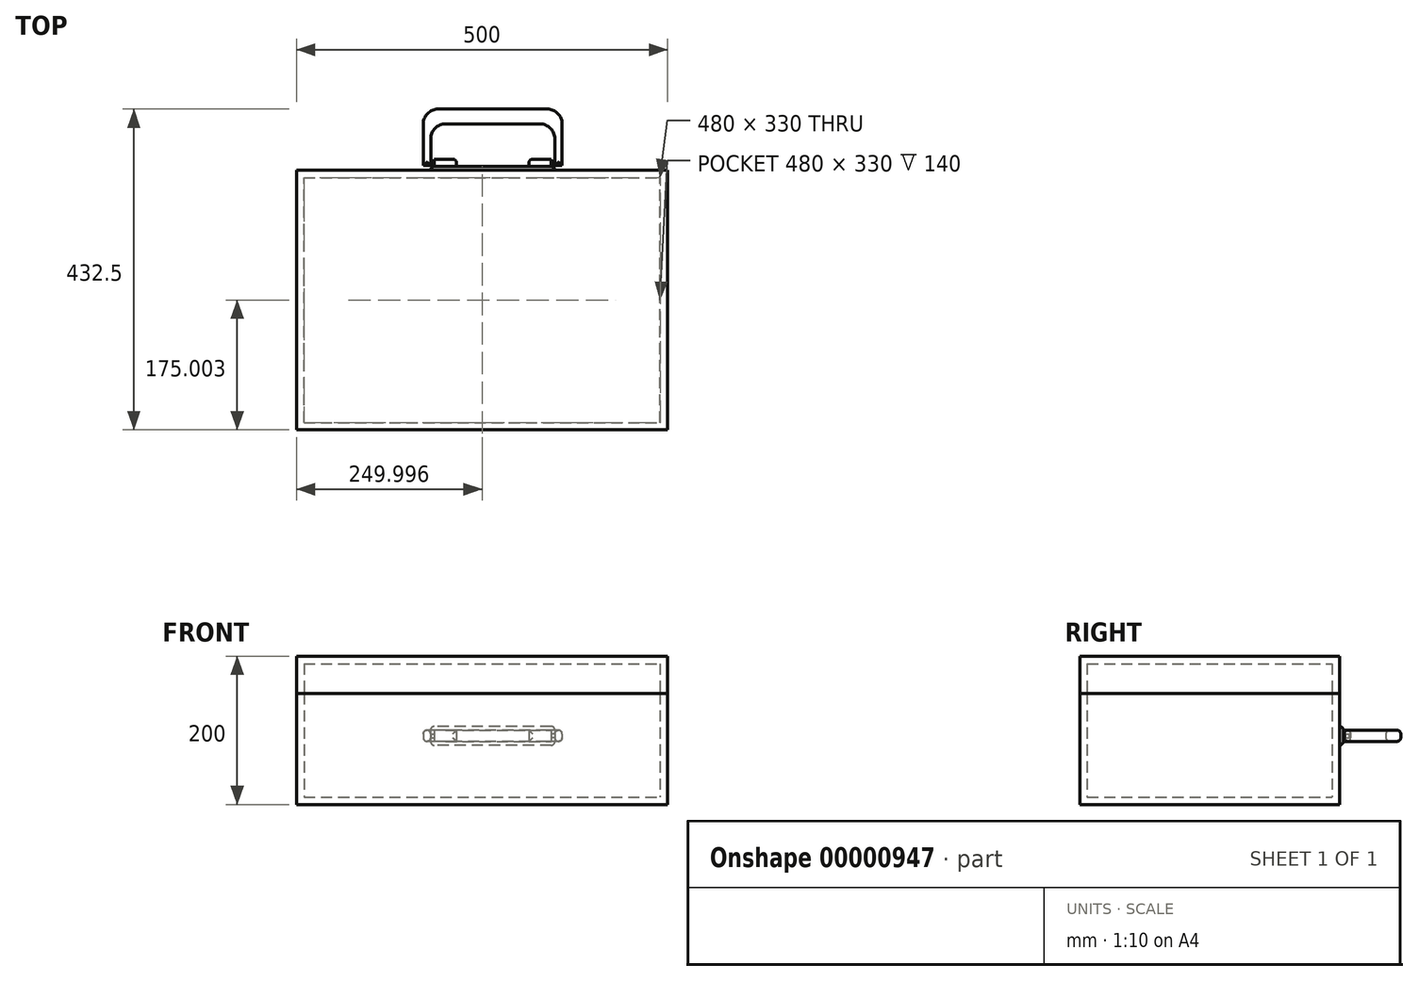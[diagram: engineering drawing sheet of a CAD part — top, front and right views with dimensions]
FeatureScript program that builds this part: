
annotation { "Feature Type Name" : "Feature", "Feature Type Description" : "" }
export const myFeature = defineFeature(function(context is Context, id is Id, definition is map)
    precondition{}
    {
        {
            var Q0;
            Q0=qCreatedBy(makeId("Top.planeOp"),FACE);
            var sketch = newSketch(context, id + "F0", { "sketchPlane" : qUnion([Q0])});
            skLineSegment(sketch, "E0.bottom", {"start": v(-264.32, -184.4) * mm, "end": v(235.68, -184.4) * mm});
            skLineSegment(sketch, "E0.top", {"start": v(-264.32, 165.6) * mm, "end": v(235.68, 165.6) * mm});
            skLineSegment(sketch, "E0.left", {"start": v(-264.32, -184.4) * mm, "end": v(-264.32, 165.6) * mm});
            skLineSegment(sketch, "E0.right", {"start": v(235.68, -184.4) * mm, "end": v(235.68, 165.6) * mm});
            skSolve(sketch);
        }
        {
            var Q0;
            Q0=makeQuery(id+"F0.imprint","IMPRINT",FACE,{"disambiguationData":[TD([[makeQuery(id+"F0.imprint","IMPRINT",EDGE,{"derivedFrom":sQuery(id+"F0.wireOp",EDGE,"E0.bottom")}),1.0]])]});
            extrude(context, id + "F1", {"entities" : qUnion([Q0]), "depth" : 150 * mm});
        }
        {
            var Q0;
            Q0=makeQuery(id+"F1.opExtrude","CAP_FACE",FACE,{"disambiguationData":[OSD([sQuery(id+"F0.wireOp",EDGE,"E0.bottom"),sQuery(id+"F0.wireOp",EDGE,"E0.top"),sQuery(id+"F0.wireOp",EDGE,"E0.left"),sQuery(id+"F0.wireOp",EDGE,"E0.right")])],"isStart":false});
            shell(context, id + "F2", {"entities" : qUnion([Q0]), "thickness" : 10 * mm});
        }
        {
            var Q0;
            Q0=makeQuery(id+"F1.opExtrude","CAP_FACE",FACE,{"disambiguationData":[OSD([sQuery(id+"F0.wireOp",EDGE,"E0.bottom"),sQuery(id+"F0.wireOp",EDGE,"E0.top"),sQuery(id+"F0.wireOp",EDGE,"E0.left"),sQuery(id+"F0.wireOp",EDGE,"E0.right")])],"isStart":false});
            var sketch = newSketch(context, id + "F3", { "sketchPlane" : qUnion([Q0])});
            skLineSegment(sketch, "E1.0", {"start": v(-264.32, 165.6) * mm, "end": v(235.68, 165.6) * mm});
            skLineSegment(sketch, "E2.0", {"start": v(-264.32, -184.4) * mm, "end": v(-264.32, 165.6) * mm});
            skLineSegment(sketch, "E3.0", {"start": v(235.68, -184.4) * mm, "end": v(235.68, 165.6) * mm});
            skLineSegment(sketch, "E4.0", {"start": v(-264.32, -184.4) * mm, "end": v(235.68, -184.4) * mm});
            skSolve(sketch);
        }
        {
            var Q0;
            {var subQ6=sQuery(id+"F0.wireOp",EDGE,"E0.bottom");var subQ7=makeQuery(id+"F3.imprint","IMPRINT",EDGE,{"derivedFrom":makeQuery(id+"F2.opShell","OFFSET_EDGE",EDGE,{"disambiguationData":[OSD([subQ6]),TDD([makeQuery(id+"F1.opExtrude","CAP_EDGE",EDGE,{"disambiguationData":[OSD([subQ6])],"isStart":false})])]})});Q0=qUnion([makeQuery(id+"F3.imprint","IMPRINT",FACE,{"disambiguationData":[TD([[makeQuery(id+"F3.imprint","IMPRINT",EDGE,{"derivedFrom":sQuery(id+"F3.wireOp",EDGE,"E1.0")}),-1.0]])]}),makeQuery(id+"F3.imprint","IMPRINT",FACE,{"disambiguationData":[TD([[subQ7,1.0]])]})]);}
            extrude(context, id + "F4", {"entities" : qUnion([Q0]), "depth" : 50 * mm});
        }
        {
            var Q0;
            Q0=makeQuery(id+"F4.opExtrude","CAP_FACE",FACE,{"disambiguationData":[OSD([sQuery(id+"F3.wireOp",EDGE,"E1.0"),sQuery(id+"F3.wireOp",EDGE,"E2.0"),sQuery(id+"F3.wireOp",EDGE,"E3.0"),sQuery(id+"F3.wireOp",EDGE,"E4.0")])],"isStart":true});
            shell(context, id + "F5", {"entities" : qUnion([Q0]), "thickness" : 10 * mm});
        }
        {
            var Q0;
            Q0=makeQuery(id+"F1.opExtrude","SWEPT_FACE",FACE,{"disambiguationData":[OSD([sQuery(id+"F0.wireOp",EDGE,"E0.top")])]});
            var sketch = newSketch(context, id + "F6", { "sketchPlane" : qUnion([Q0])});
            skLineSegment(sketch, "E5.rect.bottom", {"start": v(-78.8, 105.28) * mm, "end": v(78.8, 105.28) * mm});
            skLineSegment(sketch, "E5.rect.top", {"start": v(-78.8, 79.98) * mm, "end": v(78.8, 79.98) * mm});
            skLineSegment(sketch, "E5.rect.left", {"start": v(-83.8, 100.28) * mm, "end": v(-83.8, 84.98) * mm});
            skLineSegment(sketch, "E5.rect.right", {"start": v(83.8, 100.28) * mm, "end": v(83.8, 84.98) * mm});
            skPoint(sketch, "E5.rect.middle", {"position": v(0, 92.63) * mm});
            skPoint(sketch, "E6.visualSharp", {"position": v(-83.8, 105.28) * mm});
            skArc(sketch, "E6.filletArc", {"start": v(-78.8, 105.28) * mm, "mid": v(-82.33, 103.81) * mm, "end": v(-83.8, 100.28) * mm});
            skPoint(sketch, "E7.visualSharp", {"position": v(-83.8, 79.98) * mm});
            skArc(sketch, "E7.filletArc", {"start": v(-83.8, 84.98) * mm, "mid": v(-82.33, 81.45) * mm, "end": v(-78.8, 79.98) * mm});
            skPoint(sketch, "E8.visualSharp", {"position": v(83.8, 79.98) * mm});
            skArc(sketch, "E8.filletArc", {"start": v(78.8, 79.98) * mm, "mid": v(82.33, 81.45) * mm, "end": v(83.8, 84.98) * mm});
            skPoint(sketch, "E9.visualSharp", {"position": v(83.8, 105.28) * mm});
            skArc(sketch, "E9.filletArc", {"start": v(83.8, 100.28) * mm, "mid": v(82.33, 103.81) * mm, "end": v(78.8, 105.28) * mm});
            skLineSegment(sketch, "E10.bottom", {"start": v(-48.8, 100.28) * mm, "end": v(-78.8, 100.28) * mm});
            skLineSegment(sketch, "E10.top", {"start": v(-48.8, 84.98) * mm, "end": v(-78.8, 84.98) * mm});
            skLineSegment(sketch, "E10.left", {"start": v(-48.8, 100.28) * mm, "end": v(-48.8, 84.98) * mm});
            skLineSegment(sketch, "E10.right", {"start": v(-78.8, 100.28) * mm, "end": v(-78.8, 84.98) * mm});
            skLineSegment(sketch, "E11", {"start": v(0, 79.98) * mm, "end": v(0, 105.28) * mm, "construction": true});
            skLineSegment(sketch, "E12.0.MirrorCS", {"start": v(48.8, 84.98) * mm, "end": v(78.8, 84.98) * mm});
            skLineSegment(sketch, "E13.0.MirrorCS", {"start": v(48.8, 100.28) * mm, "end": v(48.8, 84.98) * mm});
            skLineSegment(sketch, "E14.0.MirrorCS", {"start": v(48.8, 100.28) * mm, "end": v(78.8, 100.28) * mm});
            skLineSegment(sketch, "E15.0.MirrorCS", {"start": v(78.8, 100.28) * mm, "end": v(78.8, 84.98) * mm});
            skSolve(sketch);
        }
        {
            var Q0;
            Q0=makeQuery(id+"F6.imprint","IMPRINT",FACE,{"disambiguationData":[TD([[makeQuery(id+"F6.imprint","IMPRINT",EDGE,{"derivedFrom":sQuery(id+"F6.wireOp",EDGE,"E5.rect.bottom")}),-1.0]])]});
            extrude(context, id + "F7", {"entities" : qUnion([Q0]), "depth" : 5 * mm});
        }
        {
            var Q0;
            Q0=makeQuery(id+"F6.imprint","IMPRINT",FACE,{"disambiguationData":[TD([[makeQuery(id+"F6.imprint","IMPRINT",EDGE,{"derivedFrom":sQuery(id+"F6.wireOp",EDGE,"E10.bottom")}),1.0]])]});
            var Q1;
            Q1=makeQuery(id+"F6.imprint","IMPRINT",FACE,{"disambiguationData":[TD([[makeQuery(id+"F6.imprint","IMPRINT",EDGE,{"derivedFrom":sQuery(id+"F6.wireOp",EDGE,"E12.0.MirrorCS")}),1.0]])]});
            extrude(context, id + "F8", {"entities" : qUnion([Q0, Q1]), "operationType" : NewBodyOperationType.ADD, "depth" : 15 * mm});
        }
        {
            var Q0;
            Q0=makeQuery(id+"F8.opExtrude","CAP_EDGE",EDGE,{"disambiguationData":[OSD([sQuery(id+"F6.wireOp",EDGE,"E10.top")])],"isStart":false});
            var Q1;
            Q1=makeQuery(id+"F8.opExtrude","CAP_EDGE",EDGE,{"disambiguationData":[OSD([sQuery(id+"F6.wireOp",EDGE,"E10.left")])],"isStart":false});
            var Q2;
            Q2=makeQuery(id+"F8.opExtrude","CAP_EDGE",EDGE,{"disambiguationData":[OSD([sQuery(id+"F6.wireOp",EDGE,"E10.bottom")])],"isStart":false});
            var Q3;
            Q3=makeQuery(id+"F8.opExtrude","CAP_EDGE",EDGE,{"disambiguationData":[OSD([sQuery(id+"F6.wireOp",EDGE,"E13.0.MirrorCS")])],"isStart":false});
            var Q4;
            Q4=makeQuery(id+"F8.opExtrude","CAP_EDGE",EDGE,{"disambiguationData":[OSD([sQuery(id+"F6.wireOp",EDGE,"E14.0.MirrorCS")])],"isStart":false});
            var Q5;
            Q5=makeQuery(id+"F8.opExtrude","CAP_EDGE",EDGE,{"disambiguationData":[OSD([sQuery(id+"F6.wireOp",EDGE,"E12.0.MirrorCS")])],"isStart":false});
            fillet(context, id + "F9", {"entities" : qUnion([Q0, Q1, Q2, Q3, Q4, Q5]), "radius" : 5 * mm, "allowEdgeOverflow" : false});
        }
        {
            var Q0;
            Q0=makeQuery(id+"F7.opExtrude","CAP_EDGE",EDGE,{"disambiguationData":[OSD([sQuery(id+"F6.wireOp",EDGE,"E5.rect.bottom")])],"isStart":false});
            fillet(context, id + "F10", {"entities" : qUnion([Q0]), "radius" : 5 * mm, "tangentPropagation" : true, "allowEdgeOverflow" : false});
        }
        {
            var Q0;
            Q0=makeQuery(id+"F8.opExtrude","SWEPT_FACE",FACE,{"disambiguationData":[OSD([sQuery(id+"F6.wireOp",EDGE,"E10.bottom")])]});
            var Q1;
            Q1=makeQuery(id+"F8.opExtrude","SWEPT_FACE",FACE,{"disambiguationData":[OSD([sQuery(id+"F6.wireOp",EDGE,"E10.top")])]});
            cPlane(context, id + "F11", {"entities" : qUnion([Q0, Q1]), "cplaneType" : CPlaneType.MID_PLANE, "offset" : 150 * mm, "width" : 150 * mm, "height" : 150 * mm});
        }
        {
            var Q0;
            Q0=qCreatedBy(id+"F11.planeOp",FACE);
            var sketch = newSketch(context, id + "F12", { "sketchPlane" : qUnion([Q0])});
            skLineSegment(sketch, "E16.0", {"start": v(78.8, 175.6) * mm, "end": v(78.8, 173.1) * mm});
            skLineSegment(sketch, "E17.0", {"start": v(78.8, 175.6) * mm, "end": v(78.8, 180.6) * mm});
            skLineSegment(sketch, "E18", {"start": v(78.8, 173.1) * mm, "end": v(83.58, 173.1) * mm});
            skLineSegment(sketch, "E19", {"start": v(83.58, 173.1) * mm, "end": v(83.58, 171.8) * mm});
            skLineSegment(sketch, "E20", {"start": v(83.58, 171.8) * mm, "end": v(93.58, 171.8) * mm});
            skLineSegment(sketch, "E21", {"start": v(93.58, 171.8) * mm, "end": v(93.58, 228.1) * mm});
            skLineSegment(sketch, "E22", {"start": v(73.58, 248.1) * mm, "end": v(0, 248.1) * mm});
            skLineSegment(sketch, "E23", {"start": v(0, 248.1) * mm, "end": v(0, 228.1) * mm});
            skLineSegment(sketch, "E24", {"start": v(0, 228.1) * mm, "end": v(63.58, 228.1) * mm});
            skLineSegment(sketch, "E25", {"start": v(83.58, 208.1) * mm, "end": v(83.58, 178.62) * mm});
            skLineSegment(sketch, "E26", {"start": v(83.58, 178.62) * mm, "end": v(83.58, 178.1) * mm});
            skLineSegment(sketch, "E27", {"start": v(83.58, 178.1) * mm, "end": v(78.8, 178.1) * mm});
            skLineSegment(sketch, "E28", {"start": v(0, 257.2) * mm, "end": v(0, 154.47) * mm, "construction": true});
            skLineSegment(sketch, "E29.0.MirrorCS", {"start": v(-73.58, 248.1) * mm, "end": v(0, 248.1) * mm});
            skLineSegment(sketch, "E30.0.MirrorCS", {"start": v(-93.58, 171.8) * mm, "end": v(-93.58, 228.1) * mm});
            skLineSegment(sketch, "E31.0.MirrorCS", {"start": v(-83.58, 171.8) * mm, "end": v(-93.58, 171.8) * mm});
            skLineSegment(sketch, "E32.0.MirrorCS", {"start": v(-78.8, 173.1) * mm, "end": v(-83.58, 173.1) * mm});
            skLineSegment(sketch, "E33.0.MirrorCS", {"start": v(-83.58, 173.1) * mm, "end": v(-83.58, 171.8) * mm});
            skLineSegment(sketch, "E34.0.MirrorCS", {"start": v(-83.58, 178.1) * mm, "end": v(-78.8, 178.1) * mm});
            skLineSegment(sketch, "E35.0.MirrorCS", {"start": v(-83.58, 208.1) * mm, "end": v(-83.58, 178.62) * mm});
            skLineSegment(sketch, "E36.0.MirrorCS", {"start": v(-83.58, 178.62) * mm, "end": v(-83.58, 178.1) * mm});
            skLineSegment(sketch, "E37.0.MirrorCS", {"start": v(0, 228.1) * mm, "end": v(-63.58, 228.1) * mm});
            skLineSegment(sketch, "E38.0.MirrorCS", {"start": v(-78.8, 175.6) * mm, "end": v(-78.8, 178.1) * mm});
            skLineSegment(sketch, "E39.0.MirrorCS", {"start": v(-78.8, 175.6) * mm, "end": v(-78.8, 173.1) * mm});
            skPoint(sketch, "E40.orphan", {"position": v(-78.8, 180.6) * mm});
            skLineSegment(sketch, "E41", {"start": v(-83.58, 178.1) * mm, "end": v(-83.58, 173.1) * mm});
            skLineSegment(sketch, "E42", {"start": v(83.58, 178.1) * mm, "end": v(83.58, 173.1) * mm});
            skPoint(sketch, "E43.visualSharp", {"position": v(83.58, 228.1) * mm});
            skArc(sketch, "E43.filletArc", {"start": v(83.58, 208.1) * mm, "mid": v(77.72, 222.24) * mm, "end": v(63.58, 228.1) * mm});
            skPoint(sketch, "E44.visualSharp", {"position": v(93.58, 248.1) * mm});
            skArc(sketch, "E44.filletArc", {"start": v(93.58, 228.1) * mm, "mid": v(87.72, 242.24) * mm, "end": v(73.58, 248.1) * mm});
            skPoint(sketch, "E45.visualSharp", {"position": v(-83.58, 228.1) * mm});
            skArc(sketch, "E45.filletArc", {"start": v(-63.58, 228.1) * mm, "mid": v(-77.72, 222.24) * mm, "end": v(-83.58, 208.1) * mm});
            skPoint(sketch, "E46.visualSharp", {"position": v(-93.58, 248.1) * mm});
            skArc(sketch, "E46.filletArc", {"start": v(-73.58, 248.1) * mm, "mid": v(-87.72, 242.24) * mm, "end": v(-93.58, 228.1) * mm});
            skSolve(sketch);
        }
        {
            var Q0;
            {var subQ1=sQuery(id+"F12.wireOp",EDGE,"E18");Q0=makeQuery(id+"F12.imprint","IMPRINT",FACE,{"disambiguationData":[TD([[makeQuery(id+"F12.imprint","IMPRINT",EDGE,{"derivedFrom":subQ1}),1.0]])]});}
            var Q1;
            Q1=makeQuery(id+"F12.imprint","IMPRINT",FACE,{"disambiguationData":[TD([[makeQuery(id+"F12.imprint","IMPRINT",EDGE,{"derivedFrom":sQuery(id+"F12.wireOp",EDGE,"E32.0.MirrorCS")}),-1.0]])]});
            extrude(context, id + "F13", {"entities" : qUnion([Q0, Q1]), "endBound" : BoundingType.SYMMETRIC, "depth" : 5 * mm});
        }
        {
            var Q0;
            Q0=makeQuery(id+"F12.imprint","IMPRINT",FACE,{"disambiguationData":[TD([[makeQuery(id+"F12.imprint","IMPRINT",EDGE,{"derivedFrom":sQuery(id+"F12.wireOp",EDGE,"E19")}),1.0]])]});
            var Q1;
            Q1=makeQuery(id+"F12.imprint","IMPRINT",FACE,{"disambiguationData":[TD([[makeQuery(id+"F12.imprint","IMPRINT",EDGE,{"derivedFrom":sQuery(id+"F12.wireOp",EDGE,"E23")}),-1.0]])]});
            extrude(context, id + "F14", {"entities" : qUnion([Q0, Q1]), "operationType" : NewBodyOperationType.ADD, "endBound" : BoundingType.SYMMETRIC, "depth" : 15 * mm});
        }
        {
            var Q0;
            Q0=makeQuery(id+"F14.opExtrude","CAP_FACE",FACE,{"disambiguationData":[OSD([sQuery(id+"F12.wireOp",EDGE,"E19"),sQuery(id+"F12.wireOp",EDGE,"E20"),sQuery(id+"F12.wireOp",EDGE,"E21"),sQuery(id+"F12.wireOp",EDGE,"E22"),sQuery(id+"F12.wireOp",EDGE,"E24"),sQuery(id+"F12.wireOp",EDGE,"E25"),sQuery(id+"F12.wireOp",EDGE,"E29.0.MirrorCS"),sQuery(id+"F12.wireOp",EDGE,"E30.0.MirrorCS"),sQuery(id+"F12.wireOp",EDGE,"E31.0.MirrorCS"),sQuery(id+"F12.wireOp",EDGE,"E33.0.MirrorCS"),sQuery(id+"F12.wireOp",EDGE,"E36.0.MirrorCS"),sQuery(id+"F12.wireOp",EDGE,"E37.0.MirrorCS"),sQuery(id+"F12.wireOp",EDGE,"E41"),sQuery(id+"F12.wireOp",EDGE,"E42"),sQuery(id+"F12.wireOp",EDGE,"E43.filletArc"),sQuery(id+"F12.wireOp",EDGE,"E44.filletArc"),sQuery(id+"F12.wireOp",EDGE,"E45.filletArc"),sQuery(id+"F12.wireOp",EDGE,"E46.filletArc")])],"isStart":false});
            var Q1;
            Q1=makeQuery(id+"F14.opExtrude","CAP_FACE",FACE,{"disambiguationData":[OSD([sQuery(id+"F12.wireOp",EDGE,"E19"),sQuery(id+"F12.wireOp",EDGE,"E20"),sQuery(id+"F12.wireOp",EDGE,"E21"),sQuery(id+"F12.wireOp",EDGE,"E22"),sQuery(id+"F12.wireOp",EDGE,"E24"),sQuery(id+"F12.wireOp",EDGE,"E25"),sQuery(id+"F12.wireOp",EDGE,"E29.0.MirrorCS"),sQuery(id+"F12.wireOp",EDGE,"E30.0.MirrorCS"),sQuery(id+"F12.wireOp",EDGE,"E31.0.MirrorCS"),sQuery(id+"F12.wireOp",EDGE,"E33.0.MirrorCS"),sQuery(id+"F12.wireOp",EDGE,"E36.0.MirrorCS"),sQuery(id+"F12.wireOp",EDGE,"E37.0.MirrorCS"),sQuery(id+"F12.wireOp",EDGE,"E41"),sQuery(id+"F12.wireOp",EDGE,"E42"),sQuery(id+"F12.wireOp",EDGE,"E43.filletArc"),sQuery(id+"F12.wireOp",EDGE,"E44.filletArc"),sQuery(id+"F12.wireOp",EDGE,"E45.filletArc"),sQuery(id+"F12.wireOp",EDGE,"E46.filletArc")])],"isStart":true});
            fillet(context, id + "F15", {"entities" : qUnion([Q0, Q1]), "radius" : 5 * mm, "tangentPropagation" : true, "allowEdgeOverflow" : false});
        }
    });
